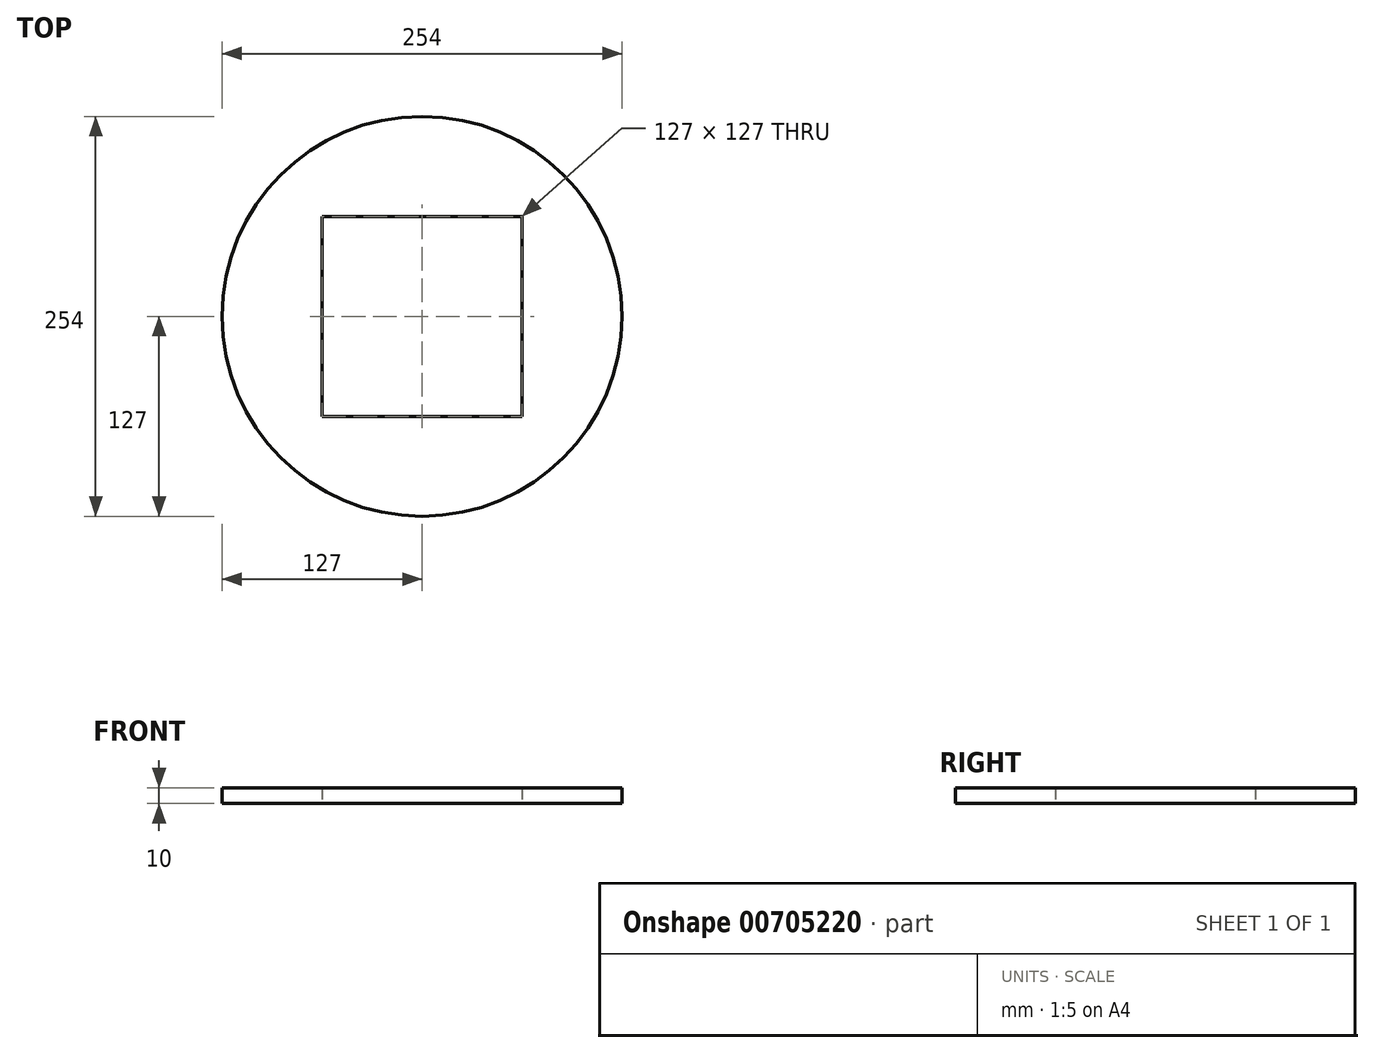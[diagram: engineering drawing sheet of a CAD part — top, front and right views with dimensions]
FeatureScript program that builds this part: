
annotation { "Feature Type Name" : "Feature", "Feature Type Description" : "" }
export const myFeature = defineFeature(function(context is Context, id is Id, definition is map)
    precondition{}
    {
        {
            var Q0;
            Q0=qCreatedBy(makeId("Top.planeOp"),FACE);
            var sketch = newSketch(context, id + "F0", { "sketchPlane" : qUnion([Q0])});
            skCircle(sketch, "E0", {"center": v(0, 0) * mm, "radius": 127 * mm});
            skLineSegment(sketch, "E1.bottom", {"start": v(63.5, 63.5) * mm, "end": v(-63.5, 63.5) * mm});
            skLineSegment(sketch, "E1.top", {"start": v(63.5, -63.5) * mm, "end": v(-63.5, -63.5) * mm});
            skLineSegment(sketch, "E1.left", {"start": v(63.5, 63.5) * mm, "end": v(63.5, -63.5) * mm});
            skLineSegment(sketch, "E1.right", {"start": v(-63.5, 63.5) * mm, "end": v(-63.5, -63.5) * mm});
            skSolve(sketch);
        }
        {
            var Q0;
            Q0=makeQuery(id+"F0.imprint","IMPRINT",FACE,{"disambiguationData":[TD([[makeQuery(id+"F0.imprint","IMPRINT",EDGE,{"derivedFrom":sQuery(id+"F0.wireOp",EDGE,"E0")}),1.0]])]});
            extrude(context, id + "F1", {"entities" : qUnion([Q0]), "depth" : 10 * mm, "offsetDistance" : 25.4 * mm});
        }
    });
